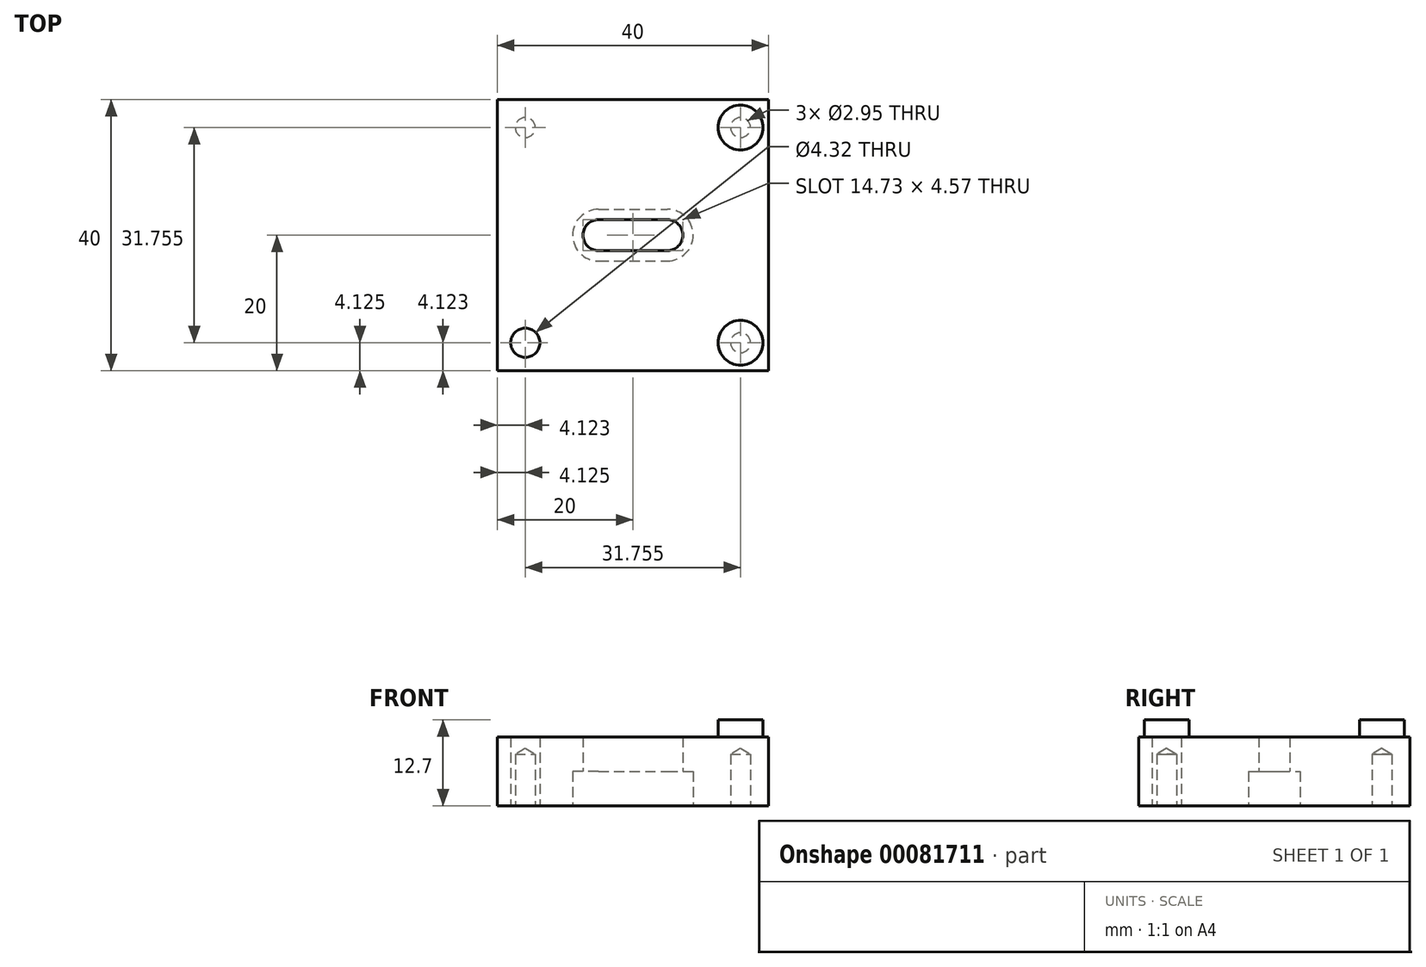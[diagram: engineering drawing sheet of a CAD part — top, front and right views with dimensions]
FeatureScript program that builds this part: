
annotation { "Feature Type Name" : "Feature", "Feature Type Description" : "" }
export const myFeature = defineFeature(function(context is Context, id is Id, definition is map)
    precondition{}
    {
        {
            var Q0;
            Q0=qCreatedBy(makeId("Top.planeOp"),FACE);
            var sketch = newSketch(context, id + "F0", { "sketchPlane" : qUnion([Q0])});
            skLineSegment(sketch, "E0.rect.bottom", {"start": v(20, 20) * mm, "end": v(-20, 20) * mm});
            skLineSegment(sketch, "E0.rect.top", {"start": v(20, -20) * mm, "end": v(-20, -20) * mm});
            skLineSegment(sketch, "E0.rect.left", {"start": v(20, 20) * mm, "end": v(20, -20) * mm});
            skLineSegment(sketch, "E0.rect.right", {"start": v(-20, 20) * mm, "end": v(-20, -20) * mm});
            skPoint(sketch, "E0.rect.middle", {"position": v(0, 0) * mm});
            skPoint(sketch, "E1", {"position": v(-15.88, 15.88) * mm});
            skCircle(sketch, "E2", {"center": v(-15.88, 15.88) * mm, "radius": 3.3 * mm});
            skCircle(sketch, "E3", {"center": v(-15.88, 15.88) * mm, "radius": 2.16 * mm});
            skCircle(sketch, "E4.MirrorC", {"center": v(15.88, 15.88) * mm, "radius": 2.16 * mm});
            skCircle(sketch, "E5.MirrorC", {"center": v(15.88, 15.88) * mm, "radius": 3.3 * mm});
            skCircle(sketch, "E6.MirrorC", {"center": v(15.88, -15.88) * mm, "radius": 2.16 * mm});
            skCircle(sketch, "E7.MirrorC", {"center": v(15.88, -15.88) * mm, "radius": 3.3 * mm});
            skCircle(sketch, "E8.MirrorC", {"center": v(-15.88, -15.88) * mm, "radius": 3.3 * mm});
            skCircle(sketch, "E9.MirrorC", {"center": v(-15.88, -15.88) * mm, "radius": 2.16 * mm});
            skLineSegment(sketch, "E10.bottom", {"start": v(20, 20) * mm, "end": v(7.62, 20) * mm});
            skLineSegment(sketch, "E10.top", {"start": v(20, -20) * mm, "end": v(7.62, -20) * mm});
            skLineSegment(sketch, "E10.right", {"start": v(7.62, 20) * mm, "end": v(7.62, -20) * mm});
            skSolve(sketch);
        }
        {
            var Q0;
            Q0=qSketchRegion(id+"F0",true);
            var Q1;
            {var subQ1=sQuery(id+"F0.wireOp",EDGE,"a0d088e4-a114-4210-b369-51a1f14ee6a4");var subQ3=makeQuery(id+"F0.imprint","IMPRINT",VERTEX,{"derivedFrom":subQ1});Q1=makeQuery(id+"F0.imprint","IMPRINT",FACE,{"disambiguationData":[TD([[makeQuery(id+"F0.imprint","IMPRINT",EDGE,{"disambiguationData":[TD([[subQ3,1.0]])],"derivedFrom":subQ1}),-1.0]])]});}
            var Q2;
            {var subQ0=sQuery(id+"F0.wireOp",EDGE,"gTe1rfOK-hWQo-2Z0q-ZLt7-7Dn1lkIVvu8e");var subQ1=sQuery(id+"F0.wireOp",EDGE,"5fa916a1-46bb-44d0-9b25-f1613092b9c4");var subQ2=makeQuery(id+"F0.imprint","INTERSECT",VERTEX,{"derivedFrom":[subQ1,subQ0]});Q2=makeQuery(id+"F0.imprint","IMPRINT",FACE,{"disambiguationData":[TD([[makeQuery(id+"F0.imprint","IMPRINT",EDGE,{"disambiguationData":[TD([[subQ2,-1.0]])],"derivedFrom":subQ1}),-1.0]])]});}
            var Q3;
            {var subQ0=sQuery(id+"F0.wireOp",EDGE,"K5YmDXpU-GgtS-j2Cr-nMIa-zNqNAAf7L4pf");var subQ1=sQuery(id+"F0.wireOp",EDGE,"f0f4ba78-e869-495a-b748-71ef774c9df5");var subQ2=makeQuery(id+"F0.imprint","INTERSECT",VERTEX,{"derivedFrom":[subQ1,subQ0]});Q3=makeQuery(id+"F0.imprint","IMPRINT",FACE,{"disambiguationData":[TD([[makeQuery(id+"F0.imprint","IMPRINT",EDGE,{"disambiguationData":[TD([[subQ2,1.0]])],"derivedFrom":subQ1}),1.0]])]});}
            var Q4;
            {var subQ0=sQuery(id+"F0.wireOp",EDGE,"K5YmDXpU-GgtS-j2Cr-nMIa-zNqNAAf7L4pf");var subQ1=sQuery(id+"F0.wireOp",EDGE,"5fa916a1-46bb-44d0-9b25-f1613092b9c4");var subQ2=makeQuery(id+"F0.imprint","INTERSECT",VERTEX,{"derivedFrom":[subQ1,subQ0]});Q4=makeQuery(id+"F0.imprint","IMPRINT",FACE,{"disambiguationData":[TD([[makeQuery(id+"F0.imprint","IMPRINT",EDGE,{"disambiguationData":[TD([[subQ2,-1.0]])],"derivedFrom":subQ1}),-1.0]])]});}
            var Q5;
            {var subQ0=sQuery(id+"F0.wireOp",EDGE,"K5YmDXpU-GgtS-j2Cr-nMIa-zNqNAAf7L4pf");var subQ1=sQuery(id+"F0.wireOp",EDGE,"5fa916a1-46bb-44d0-9b25-f1613092b9c4");var subQ2=makeQuery(id+"F0.imprint","INTERSECT",VERTEX,{"derivedFrom":[subQ1,subQ0]});Q5=makeQuery(id+"F0.imprint","IMPRINT",FACE,{"disambiguationData":[TD([[makeQuery(id+"F0.imprint","IMPRINT",EDGE,{"disambiguationData":[TD([[subQ2,-1.0]])],"derivedFrom":subQ1}),1.0]])]});}
            var Q6;
            {var subQ4=sQuery(id+"F0.wireOp",EDGE,"5fa916a1-46bb-44d0-9b25-f1613092b9c4");var subQ6=makeQuery(id+"F0.imprint","INTERSECT",VERTEX,{"derivedFrom":[subQ4,sQuery(id+"F0.wireOp",EDGE,"gTe1rfOK-hWQo-2Z0q-ZLt7-7Dn1lkIVvu8e")]});Q6=makeQuery(id+"F0.imprint","IMPRINT",FACE,{"disambiguationData":[TD([[makeQuery(id+"F0.imprint","IMPRINT",EDGE,{"disambiguationData":[TD([[subQ6,-1.0]])],"derivedFrom":subQ4}),1.0]])]});}
            var Q7;
            {var subQ0=sQuery(id+"F0.wireOp",EDGE,"rkYheQmR-etU9-h3Yq-UIZ2-16BNES9nIO10");Q7=makeQuery(id+"F0.imprint","IMPRINT",FACE,{"disambiguationData":[TD([[makeQuery(id+"F0.imprint","IMPRINT",EDGE,{"derivedFrom":subQ0}),1.0]])]});}
            var Q8;
            Q8=makeQuery(id+"F0.imprint","IMPRINT",FACE,{"disambiguationData":[TD([[makeQuery(id+"F0.imprint","IMPRINT",EDGE,{"derivedFrom":sQuery(id+"F0.wireOp",EDGE,"E2")}),1.0]])]});
            var Q9;
            Q9=makeQuery(id+"F0.imprint","IMPRINT",FACE,{"disambiguationData":[TD([[makeQuery(id+"F0.imprint","IMPRINT",EDGE,{"derivedFrom":sQuery(id+"F0.wireOp",EDGE,"E3")}),1.0]])]});
            var Q10;
            Q10=makeQuery(id+"F0.imprint","IMPRINT",FACE,{"disambiguationData":[TD([[makeQuery(id+"F0.imprint","IMPRINT",EDGE,{"derivedFrom":sQuery(id+"F0.wireOp",EDGE,"E4.MirrorC")}),1.0]])]});
            var Q11;
            Q11=makeQuery(id+"F0.imprint","IMPRINT",FACE,{"disambiguationData":[TD([[makeQuery(id+"F0.imprint","IMPRINT",EDGE,{"derivedFrom":sQuery(id+"F0.wireOp",EDGE,"E4.MirrorC")}),-1.0]])]});
            var Q12;
            Q12=makeQuery(id+"F0.imprint","IMPRINT",FACE,{"disambiguationData":[TD([[makeQuery(id+"F0.imprint","IMPRINT",EDGE,{"derivedFrom":sQuery(id+"F0.wireOp",EDGE,"E6.MirrorC")}),1.0]])]});
            var Q13;
            Q13=makeQuery(id+"F0.imprint","IMPRINT",FACE,{"disambiguationData":[TD([[makeQuery(id+"F0.imprint","IMPRINT",EDGE,{"derivedFrom":sQuery(id+"F0.wireOp",EDGE,"E6.MirrorC")}),-1.0]])]});
            var Q14;
            Q14=makeQuery(id+"F0.imprint","IMPRINT",FACE,{"disambiguationData":[TD([[makeQuery(id+"F0.imprint","IMPRINT",EDGE,{"derivedFrom":sQuery(id+"F0.wireOp",EDGE,"E8.MirrorC")}),-1.0]])]});
            var Q15;
            Q15=makeQuery(id+"F0.imprint","IMPRINT",FACE,{"disambiguationData":[TD([[makeQuery(id+"F0.imprint","IMPRINT",EDGE,{"derivedFrom":sQuery(id+"F0.wireOp",EDGE,"E9.MirrorC")}),-1.0]])]});
            extrude(context, id + "F1", {"entities" : qUnion([Q0, Q1, Q2, Q3, Q4, Q5, Q6, Q7, Q8, Q9, Q10, Q11, Q12, Q13, Q14, Q15]), "depth" : 10.16 * mm});
        }
        {
            var Q0;
            Q0=makeQuery(id+"F0.imprint","IMPRINT",FACE,{"disambiguationData":[TD([[makeQuery(id+"F0.imprint","IMPRINT",EDGE,{"derivedFrom":sQuery(id+"F0.wireOp",EDGE,"E5.MirrorC")}),1.0]])]});
            extrude(context, id + "F2", {"entities" : qUnion([Q0]), "operationType" : NewBodyOperationType.ADD, "depth" : 12.7 * mm});
        }
        {
            var Q0;
            {var subQ0=sQuery(id+"F0.wireOp",EDGE,"E8.MirrorC");var subQ1=sQuery(id+"F0.wireOp",EDGE,"E7.MirrorC");var subQ2=sQuery(id+"F0.wireOp",EDGE,"E5.MirrorC");var subQ3=sQuery(id+"F0.wireOp",EDGE,"E2");Q0=makeQuery(id+"Fgk13BH6SjzPqko_0.boolean.opBoolean","MERGE",FACE,{"derivedFrom":[makeQuery(id+"F1.opExtrude","CAP_FACE",FACE,{"disambiguationData":[OSD([sQuery(id+"F0.wireOp",EDGE,"E0.rect.bottom"),sQuery(id+"F0.wireOp",EDGE,"E0.rect.top"),sQuery(id+"F0.wireOp",EDGE,"E0.rect.right"),subQ3,subQ2,subQ1,subQ0,sQuery(id+"F0.wireOp",EDGE,"E10.bottom"),sQuery(id+"F0.wireOp",EDGE,"E10.top"),sQuery(id+"F0.wireOp",EDGE,"E0.rect.left")])],"isStart":true}),makeQuery(id+"Fgk13BH6SjzPqko_0.opExtrude","CAP_FACE",FACE,{"disambiguationData":[OSD([subQ3,sQuery(id+"F0.wireOp",EDGE,"E3")])],"isStart":true}),makeQuery(id+"Fgk13BH6SjzPqko_0.opExtrude","CAP_FACE",FACE,{"disambiguationData":[OSD([sQuery(id+"F0.wireOp",EDGE,"E4.MirrorC"),subQ2])],"isStart":true}),makeQuery(id+"Fgk13BH6SjzPqko_0.opExtrude","CAP_FACE",FACE,{"disambiguationData":[OSD([sQuery(id+"F0.wireOp",EDGE,"E6.MirrorC"),subQ1])],"isStart":true}),makeQuery(id+"Fgk13BH6SjzPqko_0.opExtrude","CAP_FACE",FACE,{"disambiguationData":[OSD([subQ0,sQuery(id+"F0.wireOp",EDGE,"E9.MirrorC")])],"isStart":true})]});}
            var sketch = newSketch(context, id + "F3", { "sketchPlane" : qUnion([Q0])});
            skCircle(sketch, "E11", {"center": v(5.08, 0) * mm, "radius": 3.81 * mm});
            skCircle(sketch, "E12", {"center": v(5.08, 0) * mm, "radius": 2.29 * mm});
            skLineSegment(sketch, "E13", {"start": v(7.62, 20) * mm, "end": v(7.62, -20) * mm, "construction": true});
            skCircle(sketch, "E14", {"center": v(-5.08, 0) * mm, "radius": 2.29 * mm});
            skCircle(sketch, "E15", {"center": v(-5.08, 0) * mm, "radius": 3.81 * mm});
            skLineSegment(sketch, "E16", {"start": v(-5.08, 2.29) * mm, "end": v(5.08, 2.29) * mm});
            skLineSegment(sketch, "E17", {"start": v(5.08, -2.29) * mm, "end": v(-5.08, -2.29) * mm});
            skLineSegment(sketch, "E18", {"start": v(-5.08, -3.81) * mm, "end": v(5.08, -3.81) * mm});
            skLineSegment(sketch, "E19", {"start": v(-5.08, 3.8) * mm, "end": v(5.08, 3.8) * mm});
            skSolve(sketch);
        }
        {
            var Q0;
            {var subQ0=sQuery(id+"F3.wireOp",EDGE,"E14");var subQ1=makeQuery(id+"F3.imprint","INTERSECT",VERTEX,{"derivedFrom":[subQ0,sQuery(id+"F3.wireOp",EDGE,"E16")]});Q0=makeQuery(id+"F3.imprint","IMPRINT",FACE,{"disambiguationData":[TD([[makeQuery(id+"F3.imprint","IMPRINT",EDGE,{"disambiguationData":[TD([[subQ1,-1.0]])],"derivedFrom":subQ0}),1.0]])]});}
            var Q1;
            {var subQ0=sQuery(id+"F3.wireOp",EDGE,"E12");var subQ1=makeQuery(id+"F3.imprint","INTERSECT",VERTEX,{"derivedFrom":[subQ0,sQuery(id+"F3.wireOp",EDGE,"E16")]});Q1=makeQuery(id+"F3.imprint","IMPRINT",FACE,{"disambiguationData":[TD([[makeQuery(id+"F3.imprint","IMPRINT",EDGE,{"disambiguationData":[TD([[subQ1,-1.0]])],"derivedFrom":subQ0}),1.0]])]});}
            var Q2;
            {var subQ0=sQuery(id+"F3.wireOp",EDGE,"E16");var subQ1=sQuery(id+"F3.wireOp",EDGE,"E14");var subQ2=makeQuery(id+"F3.imprint","INTERSECT",VERTEX,{"derivedFrom":[subQ1,subQ0]});Q2=makeQuery(id+"F3.imprint","IMPRINT",FACE,{"disambiguationData":[TD([[makeQuery(id+"F3.imprint","IMPRINT",EDGE,{"disambiguationData":[TD([[subQ2,1.0]])],"derivedFrom":subQ1}),-1.0]])]});}
            var Q3;
            {var subQ0=sQuery(id+"F3.wireOp",EDGE,"E16");var subQ1=sQuery(id+"F3.wireOp",EDGE,"E11");var subQ2=makeQuery(id+"F3.imprint","INTERSECT",VERTEX,{"derivedFrom":[subQ1,subQ0]});Q3=makeQuery(id+"F3.imprint","IMPRINT",FACE,{"disambiguationData":[TD([[makeQuery(id+"F3.imprint","IMPRINT",EDGE,{"disambiguationData":[TD([[subQ2,-1.0]])],"derivedFrom":subQ1}),-1.0]])]});}
            var Q4;
            {var subQ0=sQuery(id+"F3.wireOp",EDGE,"E16");var subQ1=sQuery(id+"F3.wireOp",EDGE,"E11");var subQ2=makeQuery(id+"F3.imprint","INTERSECT",VERTEX,{"derivedFrom":[subQ1,subQ0]});Q4=makeQuery(id+"F3.imprint","IMPRINT",FACE,{"disambiguationData":[TD([[makeQuery(id+"F3.imprint","IMPRINT",EDGE,{"disambiguationData":[TD([[subQ2,-1.0]])],"derivedFrom":subQ1}),1.0]])]});}
            extrude(context, id + "F4", {"entities" : qUnion([Q0, Q1, Q2, Q3, Q4]), "operationType" : NewBodyOperationType.REMOVE, "oppositeDirection" : true, "depth" : 25.4 * mm});
        }
        {
            var Q0;
            {var subQ0=sQuery(id+"F3.wireOp",EDGE,"E16");var subQ1=sQuery(id+"F3.wireOp",EDGE,"E14");var subQ2=makeQuery(id+"F3.imprint","INTERSECT",VERTEX,{"derivedFrom":[subQ1,subQ0]});Q0=makeQuery(id+"F3.imprint","IMPRINT",FACE,{"disambiguationData":[TD([[makeQuery(id+"F3.imprint","IMPRINT",EDGE,{"disambiguationData":[TD([[subQ2,1.0]])],"derivedFrom":subQ1}),-1.0]])]});}
            var Q1;
            {var subQ3=sQuery(id+"F3.wireOp",EDGE,"E16");var subQ4=sQuery(id+"F3.wireOp",EDGE,"E14");var subQ5=makeQuery(id+"F3.imprint","INTERSECT",VERTEX,{"derivedFrom":[subQ4,subQ3]});Q1=makeQuery(id+"F3.imprint","IMPRINT",FACE,{"disambiguationData":[TD([[makeQuery(id+"F3.imprint","IMPRINT",EDGE,{"disambiguationData":[TD([[subQ5,-1.0]])],"derivedFrom":subQ4}),-1.0]])]});}
            var Q2;
            {var subQ0=sQuery(id+"F3.wireOp",EDGE,"E19");Q2=makeQuery(id+"F3.imprint","IMPRINT",FACE,{"disambiguationData":[TD([[makeQuery(id+"F3.imprint","IMPRINT",EDGE,{"derivedFrom":subQ0}),-1.0]])]});}
            var Q3;
            {var subQ0=sQuery(id+"F3.wireOp",EDGE,"E16");var subQ1=sQuery(id+"F3.wireOp",EDGE,"E11");var subQ2=makeQuery(id+"F3.imprint","INTERSECT",VERTEX,{"derivedFrom":[subQ1,subQ0]});Q3=makeQuery(id+"F3.imprint","IMPRINT",FACE,{"disambiguationData":[TD([[makeQuery(id+"F3.imprint","IMPRINT",EDGE,{"disambiguationData":[TD([[subQ2,-1.0]])],"derivedFrom":subQ1}),-1.0]])]});}
            var Q4;
            {var subQ0=sQuery(id+"F3.wireOp",EDGE,"E16");var subQ1=sQuery(id+"F3.wireOp",EDGE,"E11");var subQ2=makeQuery(id+"F3.imprint","INTERSECT",VERTEX,{"derivedFrom":[subQ1,subQ0]});Q4=makeQuery(id+"F3.imprint","IMPRINT",FACE,{"disambiguationData":[TD([[makeQuery(id+"F3.imprint","IMPRINT",EDGE,{"disambiguationData":[TD([[subQ2,-1.0]])],"derivedFrom":subQ1}),1.0]])]});}
            var Q5;
            {var subQ5=sQuery(id+"F3.wireOp",EDGE,"E11");var subQ7=makeQuery(id+"F3.imprint","INTERSECT",VERTEX,{"derivedFrom":[subQ5,sQuery(id+"F3.wireOp",EDGE,"E19")]});Q5=makeQuery(id+"F3.imprint","IMPRINT",FACE,{"disambiguationData":[TD([[makeQuery(id+"F3.imprint","IMPRINT",EDGE,{"disambiguationData":[TD([[subQ7,-1.0]])],"derivedFrom":subQ5}),1.0]])]});}
            var Q6;
            {var subQ0=sQuery(id+"F3.wireOp",EDGE,"E18");Q6=makeQuery(id+"F3.imprint","IMPRINT",FACE,{"disambiguationData":[TD([[makeQuery(id+"F3.imprint","IMPRINT",EDGE,{"derivedFrom":subQ0}),1.0]])]});}
            extrude(context, id + "F5", {"entities" : qUnion([Q0, Q1, Q2, Q3, Q4, Q5, Q6]), "operationType" : NewBodyOperationType.REMOVE, "oppositeDirection" : true, "depth" : 5.08 * mm});
        }
        {
            var Q0;
            Q0=makeQuery(id+"F0.imprint","IMPRINT",FACE,{"disambiguationData":[TD([[makeQuery(id+"F0.imprint","IMPRINT",EDGE,{"derivedFrom":sQuery(id+"F0.wireOp",EDGE,"E4.MirrorC")}),1.0]])]});
            var Q1;
            Q1=makeQuery(id+"F0.imprint","IMPRINT",FACE,{"disambiguationData":[TD([[makeQuery(id+"F0.imprint","IMPRINT",EDGE,{"derivedFrom":sQuery(id+"F0.wireOp",EDGE,"E4.MirrorC")}),-1.0]])]});
            var Q2;
            Q2=makeQuery(id+"F0.imprint","IMPRINT",FACE,{"disambiguationData":[TD([[makeQuery(id+"F0.imprint","IMPRINT",EDGE,{"derivedFrom":sQuery(id+"F0.wireOp",EDGE,"E6.MirrorC")}),-1.0]])]});
            var Q3;
            Q3=makeQuery(id+"F0.imprint","IMPRINT",FACE,{"disambiguationData":[TD([[makeQuery(id+"F0.imprint","IMPRINT",EDGE,{"derivedFrom":sQuery(id+"F0.wireOp",EDGE,"E6.MirrorC")}),1.0]])]});
            extrude(context, id + "F6", {"entities" : qUnion([Q0, Q1, Q2, Q3]), "operationType" : NewBodyOperationType.ADD, "depth" : 12.7 * mm});
        }
        {
            var Q0;
            Q0=makeQuery(id+"F1.opExtrude","CAP_FACE",FACE,{"disambiguationData":[OSD([sQuery(id+"F0.wireOp",EDGE,"E0.rect.bottom"),sQuery(id+"F0.wireOp",EDGE,"E0.rect.top"),sQuery(id+"F0.wireOp",EDGE,"E0.rect.right"),sQuery(id+"F0.wireOp",EDGE,"E10.bottom"),sQuery(id+"F0.wireOp",EDGE,"E10.top"),sQuery(id+"F0.wireOp",EDGE,"E0.rect.left")])],"isStart":true});
            var sketch = newSketch(context, id + "F7", { "sketchPlane" : qUnion([Q0])});
            skPoint(sketch, "E20", {"position": v(-15.88, 15.88) * mm});
            skPoint(sketch, "E21.MirrorP", {"position": v(15.88, 15.88) * mm});
            skPoint(sketch, "E22.MirrorP", {"position": v(-15.88, -15.88) * mm});
            skPoint(sketch, "E23.MirrorP", {"position": v(15.88, -15.88) * mm});
            skSolve(sketch);
        }
        {
            var Q0;
            Q0=sQuery(id+"F7.wireOp",VERTEX,"E20");
            var Q1;
            Q1=sQuery(id+"F7.wireOp",VERTEX,"E21.MirrorP");
            var Q2;
            Q2=sQuery(id+"F7.wireOp",VERTEX,"E23.MirrorP");
            var Q3;
            Q3=sQuery(id+"F7.wireOp",VERTEX,"E22.MirrorP");
            var Q4;
            Q4=makeQuery(id+"F1.opExtrude","SWEPT_BODY",BODY,{"disambiguationData":[OSD([sQuery(id+"F0.wireOp",EDGE,"E0.rect.bottom"),sQuery(id+"F0.wireOp",EDGE,"E0.rect.top"),sQuery(id+"F0.wireOp",EDGE,"E0.rect.right"),sQuery(id+"F0.wireOp",EDGE,"E10.bottom"),sQuery(id+"F0.wireOp",EDGE,"E10.top"),sQuery(id+"F0.wireOp",EDGE,"E0.rect.left")])]});
            hole(context, id + "F8", {"style" : HoleStyle.SIMPLE, "endStyle" : HoleEndStyle.BLIND, "standardTappedOrClearance" : lookupTablePath({ "standard" : "ANSI", "engagement" : "50%", "pitch" : "32 tpi", "size" : "#6", "type" : "Tapped" }), "standardBlindInLast" : lookupTablePath({ "standard" : "ANSI", "engagement" : "50%", "pitch" : "32 tpi", "size" : "#6", "type" : "Tapped" }), "holeDiameter" : 2.95 * mm, "holeDepth" : 7.62 * mm, "startFromSketch" : true, "locations" : qUnion([Q0, Q1, Q2, Q3]), "scope" : qUnion([Q4]), "majorDiameter" : 3.5 * mm});
        }
    });
